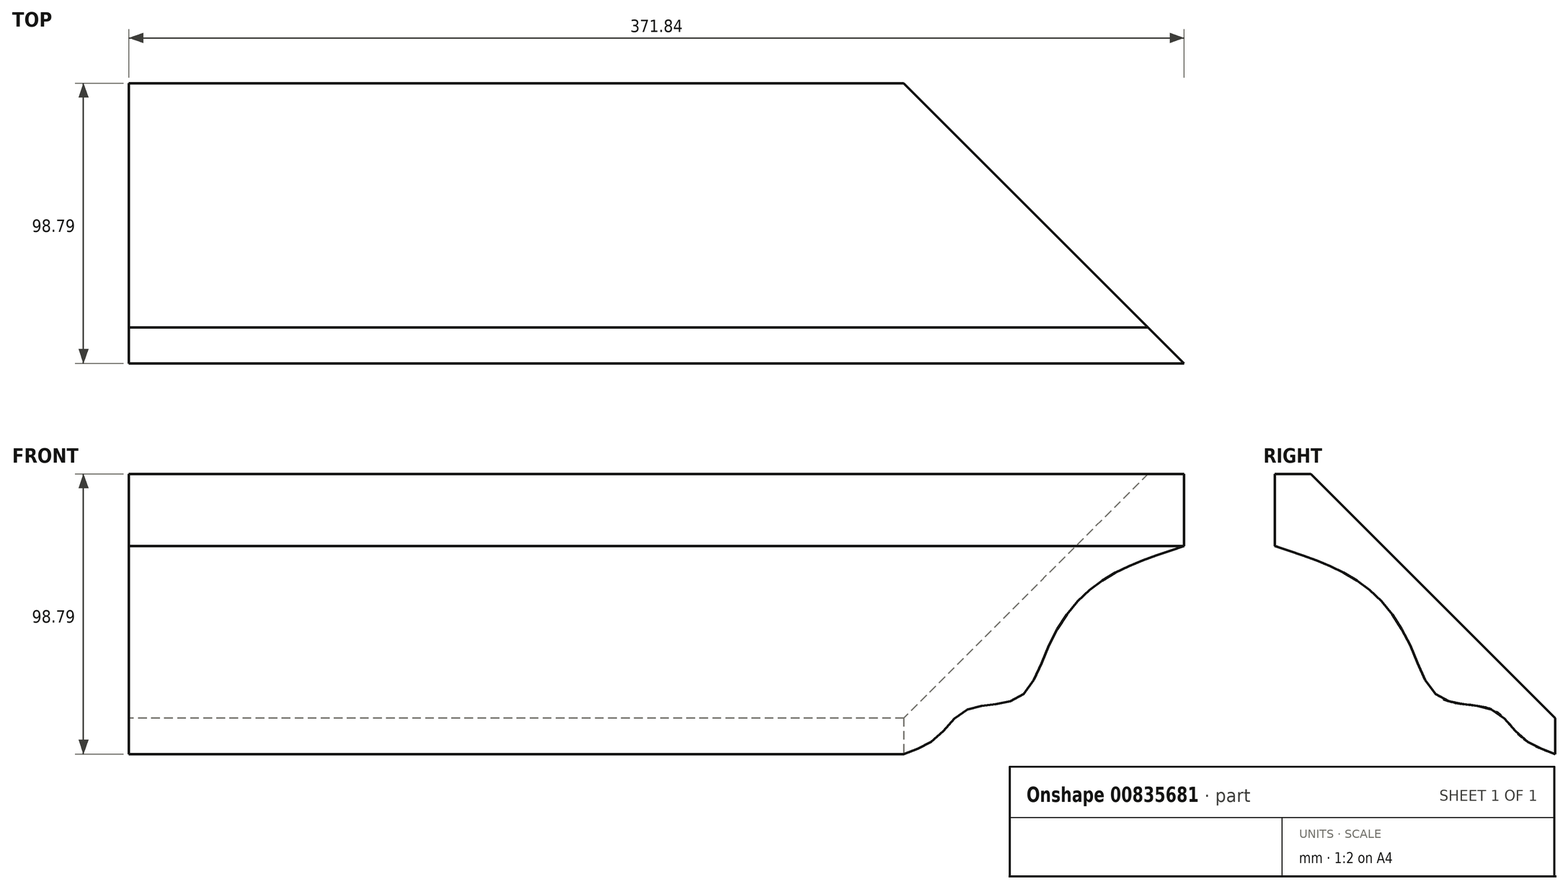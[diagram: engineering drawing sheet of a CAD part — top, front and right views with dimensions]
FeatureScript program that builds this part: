
annotation { "Feature Type Name" : "Feature", "Feature Type Description" : "" }
export const myFeature = defineFeature(function(context is Context, id is Id, definition is map)
    precondition{}
    {
        {
            var Q0;
            Q0=qCreatedBy(makeId("Right.planeOp"),FACE);
            var sketch = newSketch(context, id + "F0", { "sketchPlane" : qUnion([Q0])});
            skLineSegment(sketch, "E0", {"start": v(0, 0) * mm, "end": v(0, 12.7) * mm});
            skLineSegment(sketch, "E1", {"start": v(0, 12.7) * mm, "end": v(-86.09, 98.79) * mm});
            skLineSegment(sketch, "E2", {"start": v(-86.09, 98.79) * mm, "end": v(-98.79, 98.79) * mm});
            skLineSegment(sketch, "E3", {"start": v(-98.79, 98.79) * mm, "end": v(-98.79, 73.37) * mm});
            skFitSpline(sketch, "E4", {"points": [v(-98.79, 73.37) * mm, v(-67.03, 59.17) * mm, v(-50.62, 37.14) * mm, v(-40.3, 19.8) * mm, v(-22.03, 15.58) * mm, v(-12.19, 6.2) * mm, v(0, 0) * mm], "startDerivative": vector(161.42, -53.23) * mm, "endDerivative": vector(98.44, -35.45) * mm});
            skSolve(sketch);
        }
        {
            var Q0;
            Q0=qSketchRegion(id+"F0",true);
            extrude(context, id + "F1", {"entities" : qUnion([Q0]), "depth" : 1447.8 * mm, "offsetDistance" : 25.4 * mm});
        }
        {
            var Q0;
            Q0=qCreatedBy(makeId("Top.planeOp"),FACE);
            var sketch = newSketch(context, id + "F2", { "sketchPlane" : qUnion([Q0])});
            skLineSegment(sketch, "E5", {"start": v(0, 0) * mm, "end": v(101.6, 0) * mm});
            skLineSegment(sketch, "E6", {"start": v(101.6, 0) * mm, "end": v(0, -101.6) * mm});
            skLineSegment(sketch, "E7", {"start": v(0, -101.6) * mm, "end": v(0, 0) * mm});
            skSolve(sketch);
        }
        {
            var Q0;
            Q0=qSketchRegion(id+"F2",true);
            extrude(context, id + "F3", {"entities" : qUnion([Q0]), "operationType" : NewBodyOperationType.REMOVE, "depth" : 127 * mm, "offsetDistance" : 25.4 * mm});
        }
        {
            var Q0;
            Q0=qCreatedBy(makeId("Top.planeOp"),FACE);
            var sketch = newSketch(context, id + "F4", { "sketchPlane" : qUnion([Q0])});
            skLineSegment(sketch, "E8", {"start": v(1320.8, 0) * mm, "end": v(1542.45, 0) * mm});
            skLineSegment(sketch, "E9", {"start": v(1542.45, 0) * mm, "end": v(1542.45, -221.65) * mm});
            skLineSegment(sketch, "E10", {"start": v(1542.45, -221.65) * mm, "end": v(1320.8, 0) * mm});
            skSolve(sketch);
        }
        {
            var Q0;
            Q0=qSketchRegion(id+"F4",true);
            extrude(context, id + "F5", {"entities" : qUnion([Q0]), "operationType" : NewBodyOperationType.REMOVE, "depth" : 127 * mm, "offsetDistance" : 25.4 * mm});
        }
        {
            var Q0;
            Q0=qCreatedBy(makeId("Top.planeOp"),FACE);
            var sketch = newSketch(context, id + "F6", { "sketchPlane" : qUnion([Q0])});
            skLineSegment(sketch, "E11.bottom", {"start": v(1047.75, 0) * mm, "end": v(-227.74, 0) * mm});
            skLineSegment(sketch, "E11.top", {"start": v(1047.75, -213.06) * mm, "end": v(-227.74, -213.06) * mm});
            skLineSegment(sketch, "E11.left", {"start": v(1047.75, 0) * mm, "end": v(1047.75, -213.06) * mm});
            skLineSegment(sketch, "E11.right", {"start": v(-227.74, 0) * mm, "end": v(-227.74, -213.06) * mm});
            skSolve(sketch);
        }
        {
            var Q0;
            Q0 = qSketchRegion(id + "F6", true);
            extrude(context, id + "F7", {"entities" : qUnion([Q0]), "operationType" : NewBodyOperationType.REMOVE, "depth" : 127 * mm, "offsetDistance" : 25.4 * mm});
        }
    });
